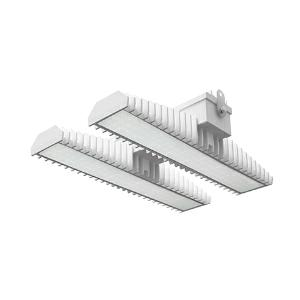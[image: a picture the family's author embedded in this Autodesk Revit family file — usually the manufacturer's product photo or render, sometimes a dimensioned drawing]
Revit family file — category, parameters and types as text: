
# Revit family: 3f_filippi_-_3f_lem_ho_ampio_3f_filippi_-_58972_a0812_-_3f_lem_2_ho_led_140_dali_cr_ampio___vs_4d01
name_source: partatom
category: Lighting Fixtures
units: mm (PartAtom-declared; Revit-internal decimal feet)

## family parameters
Cut with Voids When Loaded = No
Host = Face
Light Source = No
Part Type = Normal
Room Calculation Point = No
Round Connector Dimension = Use Diameter
Shared = No

## types (1)
- 3F Filippi - 3F LEM HO Ampio (1 x LED, 17702 lm, 138 W, 4000 K)
    Apparent Load = 138 VA
    Approval mark = CE
    CIE Flux Codes = 67 90 97 100 100
    Color Rendering = 80
    Color Temperature = 4000 K
    Control Gear = Electronic transformer
    Default Elevation = 1800 mm
    Description = Industrial luminaire with high light output and high luminous efficiency designed with the most innovative technologies for environments with temperature up to 55°C.

ILLUMINOTECHNICAL
Luminous efficiency 100% (DLOR 98%, ULOR 2%).
Initial luminous flux of the luminaire 17702 lm.
Direct symmetric wide distribution: the illuminated area has a rectangular shape.
Installation Interdistance Transv.D = 1.24 x hu - Long.D = 1.20 x hu.
Tabular UGR (CIE 117 - 4H-8H; S=0.25H; 70/50/20): RUG 23.1 - 23.1.
Beam angle: 82° - 83°.
Luminous efficacy 128 lm/W.
Lifetime (L93/B10): 30000 h. (tq+25°C)
Lifetime (L90/B10): 50000 h. (tq+25°C)
Lifetime (L85/B10): 80000 h. (tq+25°C)
Lifetime (L80/B10): 100000 h. (tq+25°C)
Lifetime (L85/B10): 50000 h. (tq+55°C)
Sudden decreased luminous flux after 50000 hours: 0% (C0).
Photobiological safety in compliance with IEC/TR 62778: RG0 risk exempt, (IEC 62471).
In compliance with IEC/EN 62722-2-1 - IEC/EN 62717 standards.

SOURCE
2 Mid-Power linear LED modules 70W/840.
Energy efficiency class (UE 2019/2020 - UE 2019/2015): C.
CIE 13.3 Colour rendering index: CRI >80 (R9 <50%).
IES TM-30 Fidelity Index: Rf = 84 Rg = 95.
CCT nominal colour temperature 4000 K.
Colour initial tolerance (MacAdam): SDCM 3.

MECHANICAL
Passive modular heatsinks in die-casted aluminium, painted in white colour.
To optimize the thermal management of the LED module, the heatsinks are oversized and provided with self-cleaning of cooling fins.
Wiring body in aluminium and galvanised steel anchored solidly to the sinks and thermally separated.
3F Lens lenses with high luminous efficiency, transparent methacrylate (PMMA), fixed to the LED modules.
Fixing brackets in stainless steel.
Luminaire with limited surface temperature. - D - (EN 60598-2-24)
Dimensions: 470x542 mm, height 133 mm. Weight 10.21 kg.
IP65 protection degree.
Mechanical strength to impacts IK06 (1 joule).
Glow-wire test resistance 650°C.

ELECTRICAL
Halogen Free DALI-2 DATI (Parts 251, 252, 253), PUSH-DIM, electronic wiring 230V-50/60Hz, power factor 0.97 at full load, THD <25%, constant output current, class I, 1 driver, 1 DALI addresse.
Power of the luminaire 138 W.
ENEC - CE.
Flicker: <4%.
Luminaire compliant with EN 60598-2-22 for power supply from a centralised emergency system CPSS (Central Power Supply System), not incorporated in the luminaire - high risk areas excluded. The default power and flux are 100% in AC and 15% in DC.
Ambient temperature from -30°C to +55°C.
Temperature class T6 max 85°C.
Quick connection via M25 5P connector with 9-13 mm tightening range.
Power unit positioned on a separate compartment by the LED module to ensure optimum temperatures of cabling components, to be inspectable and maintainable.
Relative humidity UR: <85%.

INSTALLATION
Ceiling / Suspended / Wall.
All accessories dedicated to this product are available on the Catalog and on our website www.3F-Filippi.com.

ACCESSORIES
A0812 - Anti-glare microprismatic VS moulded glass, tempered, not flammable, with sealing gasket.
One required for each light module. The pack contains 10 pieces.

APPLICATIONS
In commercial environments, exhibition and industrial areas, stores, open areas.
Environments in which it is necessary a total protection against falling fragments (eg environments with foodstuffs or machines with moving parts or with extreme temperature changes), use luminaires with polycarbonate lenses.

LIGHT MANAGEMENT
Recommended minimum setting: 10%.
The luminaire, equipped with (DALI-2 DATI) driver, can be controlled manually with 3F Easy Dim technology or automatically/manually with wired or wireless DALI/D2D control systems.
The D2D driver guarantees interoperability with other devices with the same certification by making the following information available:
Device Data (Part 251), Energy Report (Part 252), Diagnosis & Maintenance (Part 253).
In electrical systems without a regulation system (manual or automatic) and DALI bus, a suitable jumper must be made on the DA-DA terminals of the appliance.

WARNING
Fixture not suitable for cold stores with an ambient temperature <0°C and/or relative humidity >85%.
Luminaire designed for disposal/recycling at end-of-life.
Replaceable (LED only) light source by a professional. Replaceable control gear by a professional.
    Height = 133 mm  [stored 0.436352 ft]
    Lamp = 1 x LED
    Lamp Light Flux = 17702 lm
    Lamp Power = 138 W
    Lamp count = 1
    Length = 470 mm
    Lifetime = 50000 h
    Luminous efficacy = 128 lm/W
    Manufacturer = 3F Filippi
    ModVariant = No
    Model = 3F Filippi - 58972+A0812 - 3F LEM 2 HO LED 140 DALI CR AMPIO + VS
    Mounting Place = Ceiling
    Mounting Type = Pendant
    Number of Poles = 1
    OnlyDefault = Yes
    Power Factor = 1
    Product Name = 3F Filippi - 3F LEM HO Ampio
    Product group = pendant luminaire
    ProductGroupID = 9
    Protection Class = Protection class I
    Protection Degree = IP 65
    RLX_Detail_Level = 1
    RLX_Emergency_Light_Flux = 0 lm
    RLX_Emergency_Type = 0
    RLX_Emergency_Type_DB = No
    RlxData = <blob elided: 96889 chars, md5=9b63b125>
    Socket = socket
    Standby Power = 0 W
    System Light Flux = 17702 lm
    System Power = 138 W
    Type Comments = Product without accessories
    Type Image = 3f_filippi_-_lem_2__a0812.jpg
    URL = http://relux.com
    VarID = ---
    Voltage = 0 V
    Weight = 0.00 kg
    Width = 542 mm

note: [stored X ft] marks values corroborated as IEEE doubles in the binary element streams (Revit-internal decimal feet)

## geometry (parser evidence)
native form markers: Blend x4, Sweep x12
no freeform markers — native parametric forms only
